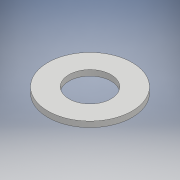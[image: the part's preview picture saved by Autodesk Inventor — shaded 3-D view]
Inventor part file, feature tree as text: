
AUTODESK INVENTOR PART (.ipt)
format: ipt  version: 2018 (Build 220112000, 112)  size: 96,768 bytes
history: native  units: mm
features: other x1, extrude x1, sketch x1
ambient origin geometry x8: Origin, YZ Plane, XZ Plane, XY Plane, X Axis, Y Axis, Z Axis, Center Point
bodies: Body1 (feature_tree)
feature tree (3):
  other  "ソリッド1"
  extrude  "押し出し1"  Depth=30.0mm
  sketch  "スケッチ1"
